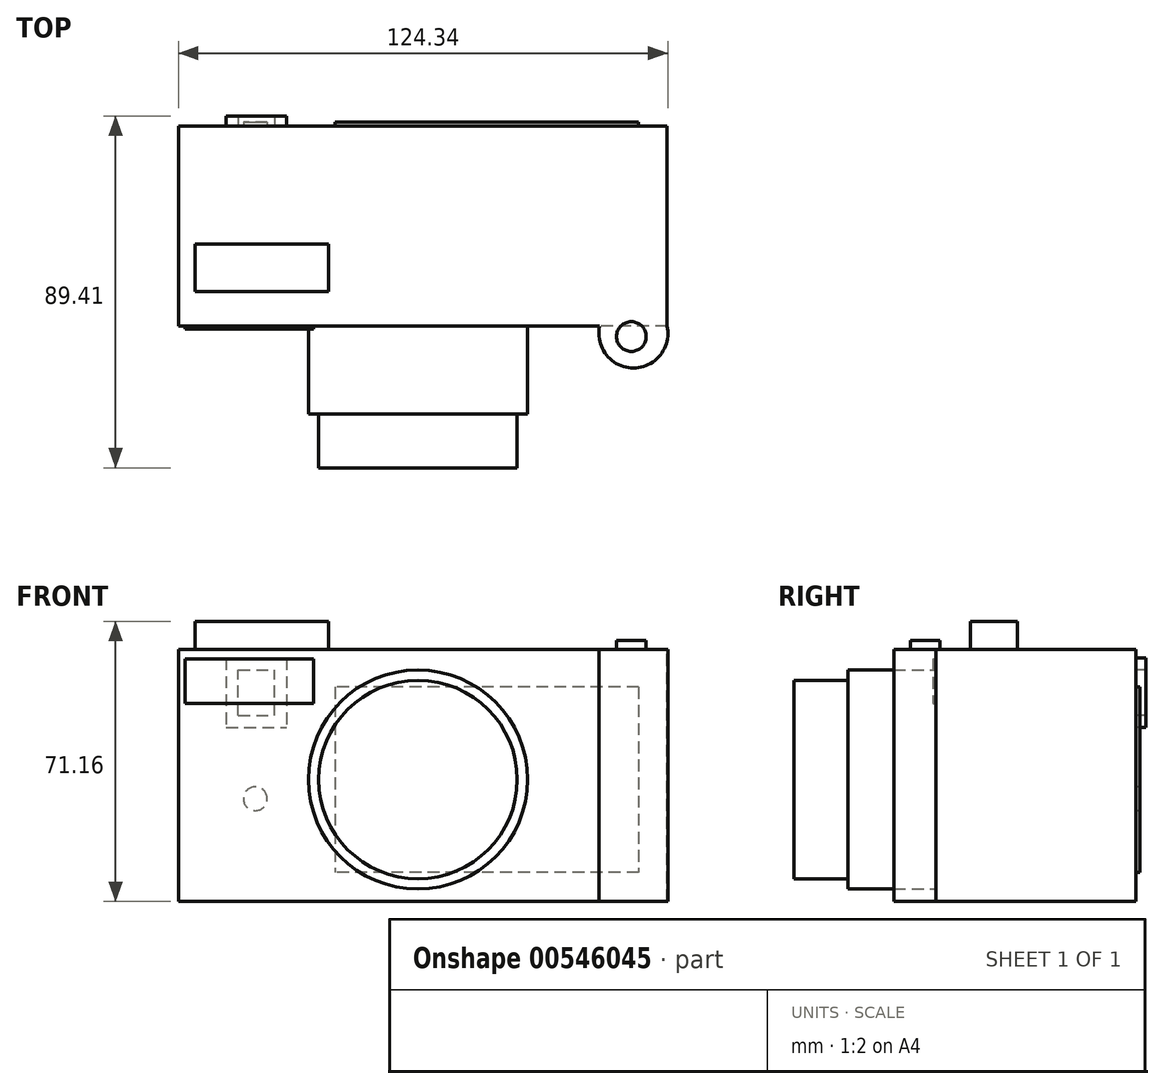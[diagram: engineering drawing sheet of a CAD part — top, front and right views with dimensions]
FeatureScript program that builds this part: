
annotation { "Feature Type Name" : "Feature", "Feature Type Description" : "" }
export const myFeature = defineFeature(function(context is Context, id is Id, definition is map)
    precondition{}
    {
        {
            var Q0;
            Q0=qCreatedBy(makeId("Front.planeOp"),FACE);
            var sketch = newSketch(context, id + "F0", { "sketchPlane" : qUnion([Q0])});
            skLineSegment(sketch, "E0.bottom", {"start": v(-60.85, 23.48) * mm, "end": v(63.3, 23.48) * mm});
            skLineSegment(sketch, "E0.top", {"start": v(-60.85, -40.57) * mm, "end": v(63.3, -40.57) * mm});
            skLineSegment(sketch, "E0.left", {"start": v(-60.85, 23.48) * mm, "end": v(-60.85, -40.57) * mm});
            skLineSegment(sketch, "E0.right", {"start": v(63.3, 23.48) * mm, "end": v(63.3, -40.57) * mm});
            skLineSegment(sketch, "E1.bottom", {"start": v(-50.71, 23.48) * mm, "end": v(-24.23, 23.48) * mm});
            skLineSegment(sketch, "E1.top", {"start": v(-50.71, 32.3) * mm, "end": v(-24.23, 32.3) * mm});
            skLineSegment(sketch, "E1.left", {"start": v(-50.71, 23.48) * mm, "end": v(-50.71, 32.3) * mm});
            skLineSegment(sketch, "E1.right", {"start": v(-24.23, 23.48) * mm, "end": v(-24.23, 32.3) * mm});
            skSolve(sketch);
        }
        {
            var Q0;
            Q0=makeQuery(id+"F0.imprint","IMPRINT",FACE,{"disambiguationData":[TD([[makeQuery(id+"F0.imprint","IMPRINT",EDGE,{"derivedFrom":sQuery(id+"F0.wireOp",EDGE,"E0.top")}),1.0]])]});
            var sketch = newSketch(context, id + "F1", { "sketchPlane" : qUnion([Q0])});
            skCircle(sketch, "E2", {"center": v(-2.63, -9.2) * mm, "radius": 26.27 * mm});
            skSolve(sketch);
        }
        {
            var Q0;
            Q0=makeQuery(id+"F1.imprint","IMPRINT",FACE,{"disambiguationData":[TD([[makeQuery(id+"F1.imprint","IMPRINT",EDGE,{"derivedFrom":sQuery(id+"F1.wireOp",EDGE,"E2")}),1.0]])]});
            extrude(context, id + "F2", {"entities" : qUnion([Q0]), "depth" : 25.4 * mm, "offsetDistance" : 25.4 * mm});
        }
        {
            var Q0;
            Q0=makeQuery(id+"F0.imprint","IMPRINT",FACE,{"disambiguationData":[TD([[makeQuery(id+"F0.imprint","IMPRINT",EDGE,{"derivedFrom":sQuery(id+"F0.wireOp",EDGE,"E0.top")}),1.0]])]});
            extrude(context, id + "F3", {"entities" : qUnion([Q0]), "operationType" : NewBodyOperationType.ADD, "oppositeDirection" : true, "depth" : 25.4 * mm, "offsetDistance" : 25.4 * mm});
        }
        {
            var Q0;
            Q0=makeQuery(id+"F3.opExtrude","CAP_FACE",FACE,{"disambiguationData":[OSD([sQuery(id+"F0.wireOp",EDGE,"E0.bottom"),sQuery(id+"F0.wireOp",EDGE,"E0.top"),sQuery(id+"F0.wireOp",EDGE,"E0.left"),sQuery(id+"F0.wireOp",EDGE,"E0.right"),sQuery(id+"F0.wireOp",EDGE,"E1.bottom")])],"isStart":true});
            extrude(context, id + "F4", {"entities" : qUnion([Q0]), "operationType" : NewBodyOperationType.ADD, "depth" : 25.4 * mm, "offsetDistance" : 25.4 * mm});
        }
        {
            var Q0;
            Q0=makeQuery(id+"F4.boolean.opBoolean","MERGE",FACE,{"derivedFrom":[makeQuery(id+"F2.opExtrude","CAP_FACE",FACE,{"disambiguationData":[OSD([sQuery(id+"F1.wireOp",EDGE,"E2")])],"isStart":false}),makeQuery(id+"F4.opExtrude","CAP_FACE",FACE,{"disambiguationData":[OSD([sQuery(id+"F0.wireOp",EDGE,"E0.bottom"),sQuery(id+"F0.wireOp",EDGE,"E0.top"),sQuery(id+"F0.wireOp",EDGE,"E0.left"),sQuery(id+"F0.wireOp",EDGE,"E0.right"),sQuery(id+"F0.wireOp",EDGE,"E1.bottom")])],"isStart":false})]});
            var sketch = newSketch(context, id + "F5", { "sketchPlane" : qUnion([Q0])});
            skCircle(sketch, "E3", {"center": v(0, -9.58) * mm, "radius": 27.83 * mm});
            skSolve(sketch);
        }
        {
            var Q0;
            Q0=makeQuery(id+"F5.imprint","IMPRINT",FACE,{"disambiguationData":[TD([[makeQuery(id+"F5.imprint","IMPRINT",EDGE,{"derivedFrom":sQuery(id+"F5.wireOp",EDGE,"E3")}),1.0]])]});
            extrude(context, id + "F6", {"entities" : qUnion([Q0]), "operationType" : NewBodyOperationType.ADD, "depth" : 22.35 * mm, "offsetDistance" : 25.4 * mm});
        }
        {
            var Q0;
            {var subQ0=sQuery(id+"F0.wireOp",EDGE,"E1.bottom");var subQ1=sQuery(id+"F0.wireOp",EDGE,"E0.bottom");Q0=makeQuery(id+"F4.boolean.opBoolean","MERGE",FACE,{"derivedFrom":[makeQuery(id+"F3.opExtrude","SWEPT_FACE",FACE,{"disambiguationData":[OSD([subQ1,subQ0])]}),makeQuery(id+"F4.opExtrude","SWEPT_FACE",FACE,{"disambiguationData":[OSD([subQ1,subQ0])]})]});}
            var sketch = newSketch(context, id + "F7", { "sketchPlane" : qUnion([Q0])});
            skSolve(sketch);
        }
        {
            var Q0;
            {var subQ0=sQuery(id+"F0.wireOp",EDGE,"E1.bottom");var subQ1=sQuery(id+"F0.wireOp",EDGE,"E0.bottom");Q0=makeQuery(id+"F7.imprint","IMPRINT",FACE,{"disambiguationData":[TD([[makeQuery(id+"F7.imprint","IMPRINT",EDGE,{"derivedFrom":makeQuery(id+"F3.opExtrude","CAP_EDGE",EDGE,{"disambiguationData":[OSD([subQ1,subQ0])],"isStart":false})}),-1.0]])]});}
            var sketch = newSketch(context, id + "F8", { "sketchPlane" : qUnion([Q0])});
            skLineSegment(sketch, "E4.bottom", {"start": v(-56.67, -4.64) * mm, "end": v(-22.72, -4.64) * mm});
            skLineSegment(sketch, "E4.top", {"start": v(-56.67, -16.64) * mm, "end": v(-22.72, -16.64) * mm});
            skLineSegment(sketch, "E4.left", {"start": v(-56.67, -4.64) * mm, "end": v(-56.67, -16.64) * mm});
            skLineSegment(sketch, "E4.right", {"start": v(-22.72, -4.64) * mm, "end": v(-22.72, -16.64) * mm});
            skSolve(sketch);
        }
        {
            var Q0;
            Q0=makeQuery(id+"F8.imprint","IMPRINT",FACE,{"disambiguationData":[TD([[makeQuery(id+"F8.imprint","IMPRINT",EDGE,{"derivedFrom":sQuery(id+"F8.wireOp",EDGE,"E4.bottom")}),-1.0]])]});
            extrude(context, id + "F9", {"entities" : qUnion([Q0]), "operationType" : NewBodyOperationType.ADD, "depth" : 7.11 * mm, "offsetDistance" : 25.4 * mm});
        }
        {
            var Q0;
            Q0=makeQuery(id+"F3.opExtrude","CAP_FACE",FACE,{"disambiguationData":[OSD([sQuery(id+"F0.wireOp",EDGE,"E0.bottom"),sQuery(id+"F0.wireOp",EDGE,"E0.top"),sQuery(id+"F0.wireOp",EDGE,"E0.left"),sQuery(id+"F0.wireOp",EDGE,"E0.right"),sQuery(id+"F0.wireOp",EDGE,"E1.bottom")])],"isStart":false});
            var sketch = newSketch(context, id + "F10", { "sketchPlane" : qUnion([Q0])});
            skLineSegment(sketch, "E5.bottom", {"start": v(-56.06, 13.91) * mm, "end": v(21.03, 13.91) * mm});
            skLineSegment(sketch, "E5.top", {"start": v(-56.06, -33.14) * mm, "end": v(21.03, -33.14) * mm});
            skLineSegment(sketch, "E5.left", {"start": v(-56.06, 13.91) * mm, "end": v(-56.06, -33.14) * mm});
            skLineSegment(sketch, "E5.right", {"start": v(21.03, 13.91) * mm, "end": v(21.03, -33.14) * mm});
            skSolve(sketch);
        }
        {
            var Q0;
            Q0=makeQuery(id+"F3.opExtrude","CAP_FACE",FACE,{"disambiguationData":[OSD([sQuery(id+"F0.wireOp",EDGE,"E0.bottom"),sQuery(id+"F0.wireOp",EDGE,"E0.top"),sQuery(id+"F0.wireOp",EDGE,"E0.left"),sQuery(id+"F0.wireOp",EDGE,"E0.right"),sQuery(id+"F0.wireOp",EDGE,"E1.bottom")])],"isStart":false});
            var sketch = newSketch(context, id + "F11", { "sketchPlane" : qUnion([Q0])});
            skCircle(sketch, "E6", {"center": v(41.32, -14.46) * mm, "radius": 5.56 * mm});
            skCircle(sketch, "E7", {"center": v(41.32, -14.46) * mm, "radius": 3.03 * mm});
            skSolve(sketch);
        }
        {
            var Q0;
            Q0=makeQuery(id+"F11.imprint","IMPRINT",FACE,{"disambiguationData":[TD([[makeQuery(id+"F11.imprint","IMPRINT",EDGE,{"derivedFrom":sQuery(id+"F11.wireOp",EDGE,"E7")}),1.0]])]});
            var sketch = newSketch(context, id + "F12", { "sketchPlane" : qUnion([Q0])});
            skSolve(sketch);
        }
        {
            var Q0;
            Q0 = qSketchRegion(id + "F12", true);
            var Q1;
            Q1=makeQuery(id+"F11.imprint","IMPRINT",FACE,{"disambiguationData":[TD([[makeQuery(id+"F11.imprint","IMPRINT",EDGE,{"derivedFrom":sQuery(id+"F11.wireOp",EDGE,"E7")}),1.0]])]});
            extrude(context, id + "F13", {"entities" : qUnion([Q0, Q1]), "operationType" : NewBodyOperationType.ADD, "depth" : 1.02 * mm, "offsetDistance" : 25.4 * mm});
        }
        {
            var Q0;
            Q0=makeQuery(id+"F3.opExtrude","CAP_FACE",FACE,{"disambiguationData":[OSD([sQuery(id+"F0.wireOp",EDGE,"E0.bottom"),sQuery(id+"F0.wireOp",EDGE,"E0.top"),sQuery(id+"F0.wireOp",EDGE,"E0.left"),sQuery(id+"F0.wireOp",EDGE,"E0.right"),sQuery(id+"F0.wireOp",EDGE,"E1.bottom")])],"isStart":false});
            var sketch = newSketch(context, id + "F14", { "sketchPlane" : qUnion([Q0])});
            skCircle(sketch, "E8", {"center": v(41.32, -14.46) * mm, "radius": 8.95 * mm});
            skSolve(sketch);
        }
        {
            var Q0;
            Q0=makeQuery(id+"F14.imprint","IMPRINT",FACE,{"disambiguationData":[TD([[makeQuery(id+"F14.imprint","IMPRINT",EDGE,{"derivedFrom":sQuery(id+"F14.wireOp",EDGE,"E8")}),1.0]])]});
            extrude(context, id + "F15", {"entities" : qUnion([Q0]), "operationType" : NewBodyOperationType.ADD, "oppositeDirection" : true, "depth" : 0.76 * mm, "offsetDistance" : 25.4 * mm});
        }
        {
            var Q0;
            Q0=makeQuery(id+"F6.opExtrude","CAP_FACE",FACE,{"disambiguationData":[OSD([sQuery(id+"F5.wireOp",EDGE,"E3")])],"isStart":false});
            var sketch = newSketch(context, id + "F16", { "sketchPlane" : qUnion([Q0])});
            skCircle(sketch, "E9", {"center": v(0, -9.58) * mm, "radius": 25.22 * mm});
            skSolve(sketch);
        }
        {
            var Q0;
            Q0=makeQuery(id+"F16.imprint","IMPRINT",FACE,{"disambiguationData":[TD([[makeQuery(id+"F16.imprint","IMPRINT",EDGE,{"derivedFrom":sQuery(id+"F16.wireOp",EDGE,"E9")}),1.0]])]});
            extrude(context, id + "F17", {"entities" : qUnion([Q0]), "operationType" : NewBodyOperationType.ADD, "depth" : 0.76 * mm, "offsetDistance" : 25.4 * mm});
        }
        {
            var Q0;
            Q0=makeQuery(id+"F3.opExtrude","CAP_FACE",FACE,{"disambiguationData":[OSD([sQuery(id+"F0.wireOp",EDGE,"E0.bottom"),sQuery(id+"F0.wireOp",EDGE,"E0.top"),sQuery(id+"F0.wireOp",EDGE,"E0.left"),sQuery(id+"F0.wireOp",EDGE,"E0.right"),sQuery(id+"F0.wireOp",EDGE,"E1.bottom")])],"isStart":false});
            var sketch = newSketch(context, id + "F18", { "sketchPlane" : qUnion([Q0])});
            skSolve(sketch);
        }
        {
            var Q0;
            {var subQ0=sQuery(id+"F0.wireOp",EDGE,"E1.bottom");var subQ1=sQuery(id+"F0.wireOp",EDGE,"E0.bottom");Q0=makeQuery(id+"FwrIUBIZqOhyNbT_1.boolean.opBoolean","MERGE",FACE,{"derivedFrom":[makeQuery(id+"F4.boolean.opBoolean","MERGE",FACE,{"derivedFrom":[makeQuery(id+"F3.opExtrude","SWEPT_FACE",FACE,{"disambiguationData":[OSD([subQ1,subQ0])]}),makeQuery(id+"F4.opExtrude","SWEPT_FACE",FACE,{"disambiguationData":[OSD([subQ1,subQ0])]})]}),makeQuery(id+"FwrIUBIZqOhyNbT_1.opExtrude","CAP_FACE",FACE,{"disambiguationData":[OSD([sQuery(id+"Fm5F4AyiNZ9wPWE_1.wireOp",EDGE,"lvfE0uTJ-Km3E-FwWz-CYbc-Oud5q9yNKGaS")])],"isStart":true})]});}
            var sketch = newSketch(context, id + "F19", { "sketchPlane" : qUnion([Q0])});
            skCircle(sketch, "E10", {"center": v(54.2, -28.09) * mm, "radius": 3.77 * mm});
            skSolve(sketch);
        }
        {
            var Q0;
            Q0=makeQuery(id+"F19.imprint","IMPRINT",FACE,{"disambiguationData":[TD([[makeQuery(id+"F19.imprint","IMPRINT",EDGE,{"derivedFrom":sQuery(id+"F19.wireOp",EDGE,"E10")}),1.0]])]});
            extrude(context, id + "F20", {"entities" : qUnion([Q0]), "operationType" : NewBodyOperationType.ADD, "depth" : 2.3 * mm, "offsetDistance" : 25.4 * mm});
        }
        {
            var Q0;
            Q0=makeQuery(id+"F4.boolean.opBoolean","MERGE",FACE,{"derivedFrom":[makeQuery(id+"F2.opExtrude","CAP_FACE",FACE,{"disambiguationData":[OSD([sQuery(id+"F1.wireOp",EDGE,"E2")])],"isStart":false}),makeQuery(id+"F4.opExtrude","CAP_FACE",FACE,{"disambiguationData":[OSD([sQuery(id+"F0.wireOp",EDGE,"E0.bottom"),sQuery(id+"F0.wireOp",EDGE,"E0.top"),sQuery(id+"F0.wireOp",EDGE,"E0.left"),sQuery(id+"F0.wireOp",EDGE,"E0.right"),sQuery(id+"F0.wireOp",EDGE,"E1.bottom")])],"isStart":false})]});
            var sketch = newSketch(context, id + "F21", { "sketchPlane" : qUnion([Q0])});
            skLineSegment(sketch, "E11.bottom", {"start": v(-59.16, 21.04) * mm, "end": v(-26.48, 21.04) * mm});
            skLineSegment(sketch, "E11.top", {"start": v(-59.16, 9.77) * mm, "end": v(-26.48, 9.77) * mm});
            skLineSegment(sketch, "E11.left", {"start": v(-59.16, 21.04) * mm, "end": v(-59.16, 9.77) * mm});
            skLineSegment(sketch, "E11.right", {"start": v(-26.48, 21.04) * mm, "end": v(-26.48, 9.77) * mm});
            skSolve(sketch);
        }
        {
            var Q0;
            Q0 = qSketchRegion(id + "F21", true);
            var Q1;
            Q1=makeQuery(id+"F21.imprint","IMPRINT",FACE,{"disambiguationData":[TD([[makeQuery(id+"F21.imprint","IMPRINT",EDGE,{"derivedFrom":sQuery(id+"F21.wireOp",EDGE,"E11.bottom")}),-1.0]])]});
            extrude(context, id + "F22", {"entities" : qUnion([Q0, Q1]), "operationType" : NewBodyOperationType.ADD, "depth" : 0.76 * mm, "offsetDistance" : 25.4 * mm});
        }
        {
            var Q0;
            {var subQ0=sQuery(id+"F0.wireOp",EDGE,"E1.bottom");var subQ1=sQuery(id+"F0.wireOp",EDGE,"E0.bottom");Q0=makeQuery(id+"F7.imprint","IMPRINT",FACE,{"disambiguationData":[TD([[makeQuery(id+"F7.imprint","IMPRINT",EDGE,{"derivedFrom":makeQuery(id+"F3.opExtrude","CAP_EDGE",EDGE,{"disambiguationData":[OSD([subQ1,subQ0])],"isStart":false})}),-1.0]])]});}
            var sketch = newSketch(context, id + "F23", { "sketchPlane" : qUnion([Q0])});
            skCircle(sketch, "E12", {"center": v(54.73, -27.3) * mm, "radius": 8.77 * mm});
            skSolve(sketch);
        }
        {
            var Q0;
            {var subQ0=sQuery(id+"F23.wireOp",EDGE,"E12");var subQ1=makeQuery(id+"F7.imprint","IMPRINT",EDGE,{"derivedFrom":makeQuery(id+"F4.opExtrude","CAP_EDGE",EDGE,{"disambiguationData":[OSD([sQuery(id+"F0.wireOp",EDGE,"E0.bottom"),sQuery(id+"F0.wireOp",EDGE,"E1.bottom")])],"isStart":false})});var subQ2=makeQuery(id+"F23.imprint","INTERSECT",VERTEX,{"disambiguationData":[OD(0.0)],"derivedFrom":[subQ1,subQ0]});Q0=makeQuery(id+"F23.imprint","IMPRINT",FACE,{"disambiguationData":[TD([[makeQuery(id+"F23.imprint","IMPRINT",EDGE,{"disambiguationData":[TD([[subQ2,-1.0]])],"derivedFrom":subQ0}),1.0]])]});}
            var Q1;
            {var subQ0=sQuery(id+"F23.wireOp",EDGE,"E12");var subQ1=makeQuery(id+"F7.imprint","IMPRINT",EDGE,{"derivedFrom":makeQuery(id+"F4.opExtrude","CAP_EDGE",EDGE,{"disambiguationData":[OSD([sQuery(id+"F0.wireOp",EDGE,"E0.bottom"),sQuery(id+"F0.wireOp",EDGE,"E1.bottom")])],"isStart":false})});var subQ2=makeQuery(id+"F23.imprint","INTERSECT",VERTEX,{"disambiguationData":[OD(0.0)],"derivedFrom":[subQ1,subQ0]});Q1=makeQuery(id+"F23.imprint","IMPRINT",FACE,{"disambiguationData":[TD([[makeQuery(id+"F23.imprint","IMPRINT",EDGE,{"disambiguationData":[TD([[subQ2,1.0]])],"derivedFrom":subQ0}),1.0]])]});}
            extrude(context, id + "F24", {"entities" : qUnion([Q0, Q1]), "operationType" : NewBodyOperationType.ADD, "oppositeDirection" : true, "depth" : 64 * mm, "offsetDistance" : 25.4 * mm});
        }
        {
            var Q0;
            Q0=makeQuery(id+"F17.opExtrude","CAP_FACE",FACE,{"disambiguationData":[OSD([sQuery(id+"F16.wireOp",EDGE,"E9")])],"isStart":false});
            extrude(context, id + "F25", {"entities" : qUnion([Q0]), "operationType" : NewBodyOperationType.ADD, "depth" : 12.95 * mm, "offsetDistance" : 25.4 * mm});
        }
        {
            var Q0;
            Q0=makeQuery(id+"F10.imprint","IMPRINT",FACE,{"disambiguationData":[TD([[makeQuery(id+"F10.imprint","IMPRINT",EDGE,{"derivedFrom":sQuery(id+"F10.wireOp",EDGE,"E5.bottom")}),-1.0]])]});
            extrude(context, id + "F26", {"entities" : qUnion([Q0]), "operationType" : NewBodyOperationType.ADD, "depth" : 1.02 * mm, "offsetDistance" : 25.4 * mm});
        }
        {
            var Q0;
            Q0=makeQuery(id+"F18.imprint","IMPRINT",FACE,{"disambiguationData":[TD([[makeQuery(id+"F18.imprint","IMPRINT",EDGE,{"derivedFrom":makeQuery(id+"F3.opExtrude","CAP_EDGE",EDGE,{"disambiguationData":[OSD([sQuery(id+"F0.wireOp",EDGE,"E0.top")])],"isStart":false})}),-1.0]])]});
            var sketch = newSketch(context, id + "F27", { "sketchPlane" : qUnion([Q0])});
            skLineSegment(sketch, "E13.bottom", {"start": v(45.64, 6.67) * mm, "end": v(36.41, 6.67) * mm});
            skLineSegment(sketch, "E13.top", {"start": v(45.64, 18.26) * mm, "end": v(36.41, 18.26) * mm});
            skLineSegment(sketch, "E13.left", {"start": v(45.64, 6.67) * mm, "end": v(45.64, 18.26) * mm});
            skLineSegment(sketch, "E13.right", {"start": v(36.41, 6.67) * mm, "end": v(36.41, 18.26) * mm});
            skPoint(sketch, "E13.middle", {"position": v(41.03, 12.46) * mm});
            skLineSegment(sketch, "E14.bottom", {"start": v(48.73, 21.26) * mm, "end": v(33.33, 21.26) * mm});
            skLineSegment(sketch, "E14.top", {"start": v(48.73, 3.66) * mm, "end": v(33.33, 3.66) * mm});
            skLineSegment(sketch, "E14.left", {"start": v(48.73, 21.26) * mm, "end": v(48.73, 3.66) * mm});
            skLineSegment(sketch, "E14.right", {"start": v(33.33, 21.26) * mm, "end": v(33.33, 3.66) * mm});
            skSolve(sketch);
        }
        {
            var Q0;
            Q0=makeQuery(id+"F27.imprint","IMPRINT",FACE,{"disambiguationData":[TD([[makeQuery(id+"F27.imprint","IMPRINT",EDGE,{"derivedFrom":sQuery(id+"F27.wireOp",EDGE,"E13.bottom")}),1.0]])]});
            extrude(context, id + "F28", {"entities" : qUnion([Q0]), "operationType" : NewBodyOperationType.ADD, "depth" : 2.54 * mm, "offsetDistance" : 25.4 * mm});
        }
    });
